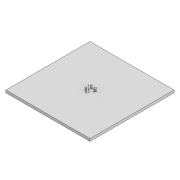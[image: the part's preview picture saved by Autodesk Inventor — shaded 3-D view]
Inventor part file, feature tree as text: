
AUTODESK INVENTOR PART (.ipt)
format: ipt  version: 2021 (Build 250183000, 183)  size: 108,544 bytes
history: native  units: in
note: dims shown in document units (in); Inventor stores cm internally (conversion verified against a paired STEP export)
features: extrude x2, sketch x2, projected_geometry x1
ambient origin geometry x8: Origin, YZ Plane, XZ Plane, XY Plane, X Axis, Y Axis, Z Axis, Center Point
bodies: Solid1 (feature_tree)
feature tree (5):
  extrude  "Extrusion1"  Depth=3937.0079in
  extrude  "Extrusion2"  Depth=118.1102in
  sketch  "Sketch1"  dims[d0=3937.0079in d1=3937.0079in]
  sketch  "Sketch2"  dims[d2=118.1102in d3=0.0in d4=78.7402in d5=118.1102in d6=78.7402in d7=31.4961in d8=118.1102in d9=59.0551in d10=118.1102in d11=78.7402in d13=157.4803in d14=31.4961in d15=39.3701in d16=118.1102in d17=78.7402in d18=98.4252in d19=39.3701in d20=39.3701in d21=196.8504in d22=23.622in d23=118.1102in d24=0.0in]
  projected_geometry  "Projected Loop1"
